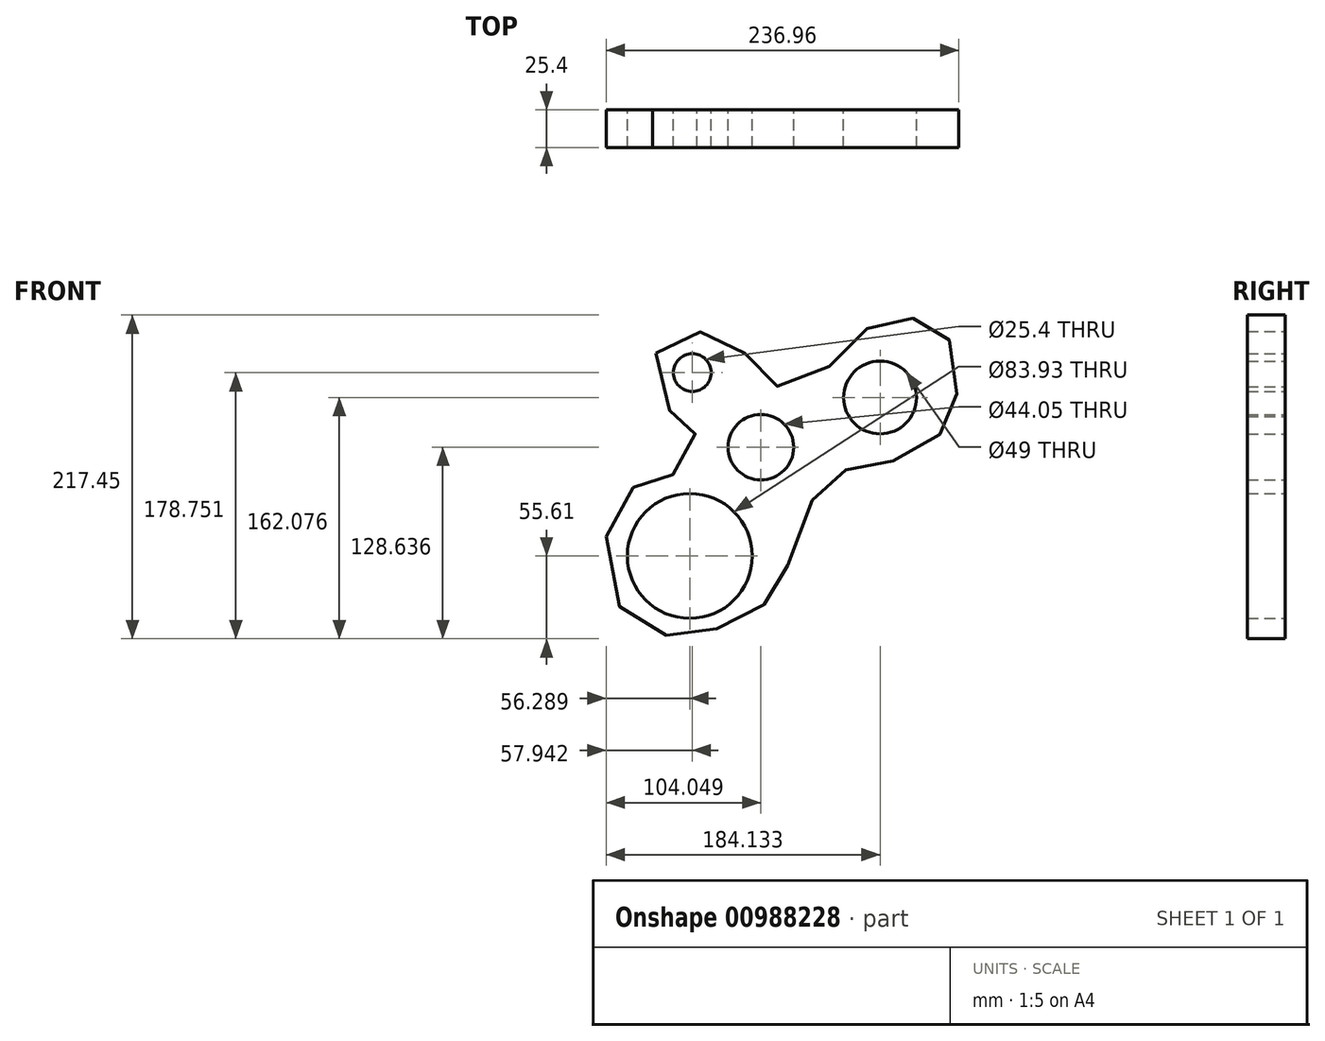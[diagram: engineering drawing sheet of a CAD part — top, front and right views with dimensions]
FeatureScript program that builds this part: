
annotation { "Feature Type Name" : "Feature", "Feature Type Description" : "" }
export const myFeature = defineFeature(function(context is Context, id is Id, definition is map)
    precondition{}
    {
        {
            var Q0;
            Q0=qCreatedBy(makeId("Front.planeOp"),FACE);
            var sketch = newSketch(context, id + "F0", { "sketchPlane" : qUnion([Q0])});
            skFitSpline(sketch, "E0", {"points": [v(-114.88, 42.49) * mm, v(-96.34, 56.03) * mm, v(-78.67, 55.53) * mm, v(-57.98, 46.41) * mm, v(-51.08, 32.89) * mm, v(-34.7, 20.37) * mm, v(-12.29, 25.55) * mm, v(10.13, 40.21) * mm, v(24.35, 56.39) * mm, v(46.34, 67.9) * mm, v(59.7, 65.3) * mm, v(76.94, 58.2) * mm, v(82.98, 50.03) * mm, v(88.58, 30.96) * mm, v(83.41, 0) * mm, v(79.1, -7.56) * mm, v(67.9, -21.14) * mm, v(43.75, -30.26) * mm, v(36.42, -32.38) * mm, v(9.7, -36.64) * mm, v(0, -42.96) * mm, v(-14.87, -66.15) * mm, v(-26.94, -101.96) * mm, v(-31.25, -111.83) * mm, v(-45.05, -129.6) * mm, v(-56.68, -136.84) * mm, v(-92.9, -148.6) * mm, v(-101.08, -148.8) * mm, v(-136.43, -135.3) * mm, v(-139.45, -125.82) * mm, v(-148.07, -83.48) * mm, v(-140.74, -56.36) * mm, v(-121.77, -43.56) * mm, v(-114.02, -41.32) * mm, v(-94.62, -35.29) * mm, v(-87.29, -18.09) * mm, v(-95.05, 0) * mm, v(-99.36, 0) * mm, v(-111.86, 12.32) * mm, v(-114.88, 42.49) * mm]});
            skLineSegment(sketch, "E1", {"start": v(-186.24, 47.42) * mm, "end": v(-190.88, -142) * mm, "construction": true});
            skSolve(sketch);
        }
        {
            var Q0;
            Q0=makeQuery(id+"F0.imprint","IMPRINT",FACE,{"disambiguationData":[TD([[makeQuery(id+"F0.imprint","IMPRINT",EDGE,{"derivedFrom":sQuery(id+"F0.wireOp",EDGE,"E0")}),-1.0]])]});
            extrude(context, id + "F1", {"entities" : qUnion([Q0]), "depth" : 25.4 * mm, "offsetDistance" : 25.4 * mm});
        }
        {
            var Q0;
            Q0=qCreatedBy(makeId("Front.planeOp"),FACE);
            var sketch = newSketch(context, id + "F2", { "sketchPlane" : qUnion([Q0])});
            skCircle(sketch, "E2", {"center": v(-90.36, 29.36) * mm, "radius": 11.65 * mm});
            skCircle(sketch, "E3", {"center": v(35.83, 12.69) * mm, "radius": 24.5 * mm});
            skCircle(sketch, "E4", {"center": v(-44.25, -20.75) * mm, "radius": 22.02 * mm});
            skCircle(sketch, "E5", {"center": v(-92.01, -93.78) * mm, "radius": 41.96 * mm});
            skSolve(sketch);
        }
        {
            var Q0;
            Q0=sQuery(id+"F2.wireOp",VERTEX,"E2.center");
            var Q1;
            Q1=makeQuery(id+"F1.opExtrude","SWEPT_BODY",BODY,{"disambiguationData":[OSD([sQuery(id+"F0.wireOp",EDGE,"E0")])]});
            hole(context, id + "F3", {"style" : HoleStyle.SIMPLE, "endStyle" : HoleEndStyle.THROUGH, "oppositeDirection" : true, "holeDiameter" : 25.4 * mm, "majorDiameter" : 6.35 * mm, "isTappedThrough" : true, "tappedDepth" : 12.7 * mm, "tapClearance" : 3, "startFromSketch" : true, "locations" : qUnion([Q0]), "scope" : qUnion([Q1])});
        }
        {
            var Q0;
            Q0=makeQuery(id+"F2.imprint","IMPRINT",FACE,{"disambiguationData":[TD([[makeQuery(id+"F2.imprint","IMPRINT",EDGE,{"derivedFrom":sQuery(id+"F2.wireOp",EDGE,"E3")}),1.0]])]});
            var Q1;
            Q1=makeQuery(id+"F2.imprint","IMPRINT",FACE,{"disambiguationData":[TD([[makeQuery(id+"F2.imprint","IMPRINT",EDGE,{"derivedFrom":sQuery(id+"F2.wireOp",EDGE,"E4")}),1.0]])]});
            var Q2;
            Q2=makeQuery(id+"F2.imprint","IMPRINT",FACE,{"disambiguationData":[TD([[makeQuery(id+"F2.imprint","IMPRINT",EDGE,{"derivedFrom":sQuery(id+"F2.wireOp",EDGE,"E5")}),1.0]])]});
            extrude(context, id + "F4", {"entities" : qUnion([Q0, Q1, Q2]), "operationType" : NewBodyOperationType.REMOVE, "depth" : 360.93 * mm, "offsetDistance" : 25.4 * mm});
        }
    });
